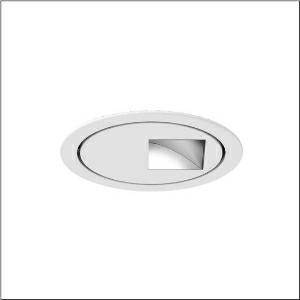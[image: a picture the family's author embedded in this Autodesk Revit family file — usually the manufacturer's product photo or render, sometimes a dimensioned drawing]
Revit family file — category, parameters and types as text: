
# Revit family: lunis_11_mini_round_51dk11b72wf21
name_source: partatom
category: Lighting Fixtures
units: mm (PartAtom-declared; Revit-internal decimal feet)

## family parameters
Cut with Voids When Loaded = No
Host = Face
Light Source = No
Part Type = Normal
Room Calculation Point = No
Round Connector Dimension = Use Diameter
Shared = No

## types (1)
- Lunis 11 mini round (1 x LED 3000K / CRI = 80 (unbekannt), 2380 lm, 3000K)
    Apparent Load = 28 VA
    CIE Flux Codes = 44 77 97 100 100
    Color Rendering = 80
    Color Temperature = 3000K
    Default Elevation = 1800 mm
    Description = Lunis 11 mini round, downlight, light control with wallwasher, of highly reflective aluminium, highly specular, light emission: direct distribution, LED rated luminous flux: 2.380lm, light colour: 830, control gear: ECG, with terminal, 3-pole, mains connection: 220..230V, AC/DC, 0/50..60Hz, LED module, luminaire module, of aluminium, highly specular, white, diameter: 176mm, clamping range: 1..40mm, recessing ring, of plastic, traffic white (RAL 9016), protection rating (complete): IP20, insulation class (complete): insulation class II (safety insulation), certification: CE, permissible ambient temperature for indoor applications: 0..+35°C, packaging unit: 1 piece
    Height = 0 mm  [stored 0 ft]
    Lamp = 1 x LED 3000K / CRI >= 80 (unbekannt)
    Lamp Light Flux = 2380 lm
    Lamp count = 1
    Length = 176 mm
    Luminous efficacy = 85 lm/W
    Manufacturer = Siteco
    ModVariant = No
    Model = 51DK11B72WF21
    Mounting Place = Ceiling
    Mounting Type = Recessed
    Number of Poles = 1
    OnlyDefault = Yes
    Power Factor = 1
    Product Name = Lunis 11 mini round
    Product group = downlight
    ProductGroupID = 401
    Protection Class = Protection class II
    Protection Degree = IP 20
    RLX_Detail_Level = 1
    RLX_Emergency_Light_Flux = 0 lm
    RLX_Emergency_Type = 0
    RLX_Emergency_Type_DB = No
    RlxData = <blob elided: 59197 chars, md5=88c8b1a7>
    Socket = socket
    Standby Power = 0 W
    System Light Flux = 2380 lm
    System Power = 28 W
    Type Comments = Product without accessories
    Type Image = l_1004772.jpg
    URL = http://relux.com
    VarID = ---
    Voltage = 0 V
    Weight = 0.00 kg
    Width = 176 mm

note: [stored X ft] marks values corroborated as IEEE doubles in the binary element streams (Revit-internal decimal feet)

## geometry (parser evidence)
native form markers: Blend x4, Sweep x11
no freeform markers — native parametric forms only
